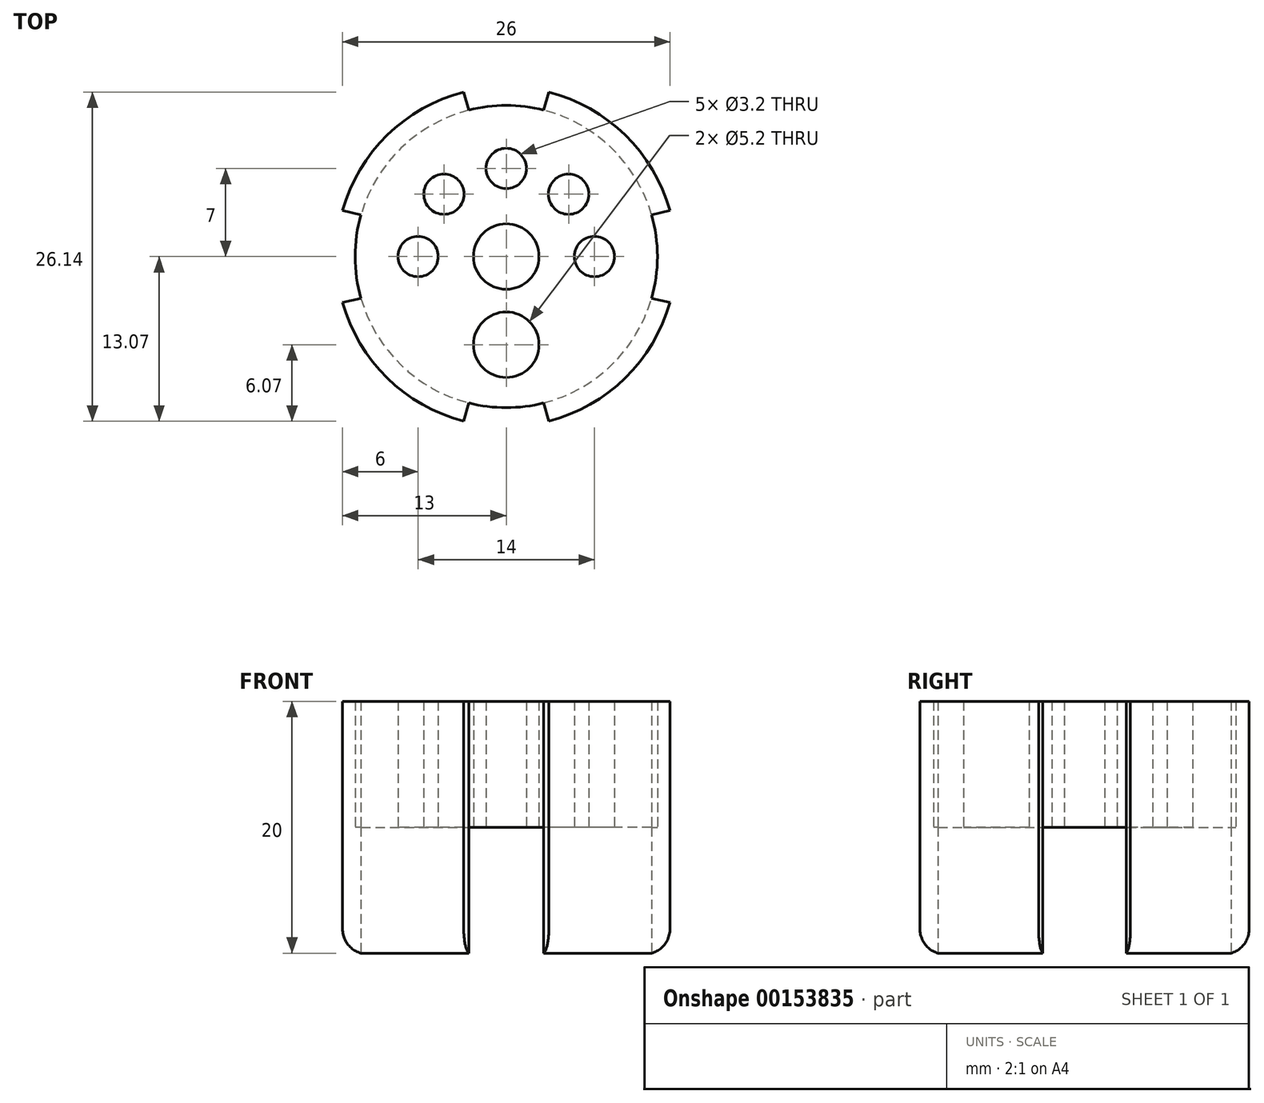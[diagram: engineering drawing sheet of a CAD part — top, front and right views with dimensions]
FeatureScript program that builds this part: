
annotation { "Feature Type Name" : "Feature", "Feature Type Description" : "" }
export const myFeature = defineFeature(function(context is Context, id is Id, definition is map)
    precondition{}
    {
        {
            var Q0;
            Q0=qCreatedBy(makeId("Top.planeOp"),FACE);
            var sketch = newSketch(context, id + "F0", { "sketchPlane" : qUnion([Q0])});
            skCircle(sketch, "E0", {"center": v(0, 0) * mm, "radius": 12 * mm});
            skCircle(sketch, "E1", {"center": v(0, 0) * mm, "radius": 10.25 * mm});
            skCircle(sketch, "E2", {"center": v(0, 0) * mm, "radius": 4.25 * mm});
            skCircle(sketch, "E3", {"center": v(0, 0) * mm, "radius": 2.6 * mm});
            skCircle(sketch, "E4", {"center": v(0, -7) * mm, "radius": 2.6 * mm});
            skCircle(sketch, "E5", {"center": v(0, 0) * mm, "radius": 7 * mm, "construction": true});
            skCircle(sketch, "E6", {"center": v(-7, 0) * mm, "radius": 1.6 * mm});
            skCircle(sketch, "E7", {"center": v(7, 0) * mm, "radius": 1.6 * mm});
            skCircle(sketch, "E8", {"center": v(0, 7) * mm, "radius": 1.6 * mm});
            skCircle(sketch, "E9", {"center": v(4.95, 4.95) * mm, "radius": 1.6 * mm});
            skCircle(sketch, "E10.MirrorC", {"center": v(-4.95, 4.95) * mm, "radius": 1.6 * mm});
            skCircle(sketch, "E11", {"center": v(0, 0) * mm, "radius": 13.5 * mm});
            skLineSegment(sketch, "E12", {"start": v(-3.38, 13.07) * mm, "end": v(-2.98, 11.62) * mm});
            skLineSegment(sketch, "E13", {"start": v(-13, 3.65) * mm, "end": v(-11.53, 3.32) * mm});
            skLineSegment(sketch, "E14.MirrorCS", {"start": v(3.38, 13.07) * mm, "end": v(2.98, 11.62) * mm});
            skLineSegment(sketch, "E15.MirrorCS", {"start": v(13, 3.65) * mm, "end": v(11.53, 3.32) * mm});
            skLineSegment(sketch, "E16.MirrorCS", {"start": v(-13, -3.65) * mm, "end": v(-11.53, -3.32) * mm});
            skLineSegment(sketch, "E17.MirrorCS", {"start": v(-3.38, -13.07) * mm, "end": v(-2.98, -11.62) * mm});
            skLineSegment(sketch, "E18.MirrorCS", {"start": v(3.38, -13.07) * mm, "end": v(2.98, -11.62) * mm});
            skLineSegment(sketch, "E19.MirrorCS", {"start": v(13, -3.65) * mm, "end": v(11.53, -3.32) * mm});
            skSolve(sketch);
        }
        {
            var Q0;
            Q0=makeQuery(id+"F0.imprint","IMPRINT",FACE,{"disambiguationData":[TD([[makeQuery(id+"F0.imprint","IMPRINT",EDGE,{"derivedFrom":sQuery(id+"F0.wireOp",EDGE,"E2")}),1.0]])]});
            extrude(context, id + "F1", {"entities" : qUnion([Q0]), "depth" : 10 * mm});
        }
        {
            var Q0;
            Q0=makeQuery(id+"F0.imprint","IMPRINT",FACE,{"disambiguationData":[TD([[makeQuery(id+"F0.imprint","IMPRINT",EDGE,{"derivedFrom":sQuery(id+"F0.wireOp",EDGE,"E1")}),1.0]])]});
            extrude(context, id + "F2", {"entities" : qUnion([Q0]), "operationType" : NewBodyOperationType.ADD, "depth" : 10 * mm});
        }
        {
            var Q0;
            Q0=makeQuery(id+"F0.imprint","IMPRINT",FACE,{"disambiguationData":[TD([[makeQuery(id+"F0.imprint","IMPRINT",EDGE,{"derivedFrom":sQuery(id+"F0.wireOp",EDGE,"E0")}),1.0]])]});
            extrude(context, id + "F3", {"entities" : qUnion([Q0]), "operationType" : NewBodyOperationType.ADD, "depth" : 10 * mm});
        }
        {
            var Q0;
            {var subQ0=sQuery(id+"F0.wireOp",EDGE,"E14.MirrorCS");Q0=makeQuery(id+"F0.imprint","IMPRINT",FACE,{"disambiguationData":[TD([[makeQuery(id+"F0.imprint","IMPRINT",EDGE,{"derivedFrom":subQ0}),1.0]])]});}
            var Q1;
            {var subQ0=sQuery(id+"F0.wireOp",EDGE,"E12");Q1=makeQuery(id+"F0.imprint","IMPRINT",FACE,{"disambiguationData":[TD([[makeQuery(id+"F0.imprint","IMPRINT",EDGE,{"derivedFrom":subQ0}),-1.0]])]});}
            var Q2;
            {var subQ0=sQuery(id+"F0.wireOp",EDGE,"E16.MirrorCS");Q2=makeQuery(id+"F0.imprint","IMPRINT",FACE,{"disambiguationData":[TD([[makeQuery(id+"F0.imprint","IMPRINT",EDGE,{"derivedFrom":subQ0}),-1.0]])]});}
            var Q3;
            {var subQ0=sQuery(id+"F0.wireOp",EDGE,"E18.MirrorCS");Q3=makeQuery(id+"F0.imprint","IMPRINT",FACE,{"disambiguationData":[TD([[makeQuery(id+"F0.imprint","IMPRINT",EDGE,{"derivedFrom":subQ0}),-1.0]])]});}
            extrude(context, id + "F4", {"entities" : qUnion([Q0, Q1, Q2, Q3]), "operationType" : NewBodyOperationType.ADD, "endBound" : BoundingType.SYMMETRIC, "depth" : 20 * mm});
        }
        {
            var Q0;
            {var subQ0=sQuery(id+"F0.wireOp",EDGE,"E11");Q0=makeQuery(id+"F4.opExtrude","CAP_EDGE",EDGE,{"disambiguationData":[OSD([subQ0]),TDD([makeQuery(id+"F0.imprint","IMPRINT",EDGE,{"disambiguationData":[TD([[makeQuery(id+"F0.imprint","INTERSECT",VERTEX,{"derivedFrom":[subQ0,sQuery(id+"F0.wireOp",EDGE,"E14.MirrorCS")]}),1.0]])],"derivedFrom":subQ0})])],"isStart":true});}
            var Q1;
            {var subQ0=sQuery(id+"F0.wireOp",EDGE,"E11");Q1=makeQuery(id+"F4.opExtrude","CAP_EDGE",EDGE,{"disambiguationData":[OSD([subQ0]),TDD([makeQuery(id+"F0.imprint","IMPRINT",EDGE,{"disambiguationData":[TD([[makeQuery(id+"F0.imprint","INTERSECT",VERTEX,{"derivedFrom":[subQ0,sQuery(id+"F0.wireOp",EDGE,"E12")]}),-1.0]])],"derivedFrom":subQ0})])],"isStart":true});}
            var Q2;
            {var subQ0=sQuery(id+"F0.wireOp",EDGE,"E11");Q2=makeQuery(id+"F4.opExtrude","CAP_EDGE",EDGE,{"disambiguationData":[OSD([subQ0]),TDD([makeQuery(id+"F0.imprint","IMPRINT",EDGE,{"disambiguationData":[TD([[makeQuery(id+"F0.imprint","INTERSECT",VERTEX,{"derivedFrom":[subQ0,sQuery(id+"F0.wireOp",EDGE,"E16.MirrorCS")]}),-1.0]])],"derivedFrom":subQ0})])],"isStart":true});}
            var Q3;
            {var subQ0=sQuery(id+"F0.wireOp",EDGE,"E11");Q3=makeQuery(id+"F4.opExtrude","CAP_EDGE",EDGE,{"disambiguationData":[OSD([subQ0]),TDD([makeQuery(id+"F0.imprint","IMPRINT",EDGE,{"disambiguationData":[TD([[makeQuery(id+"F0.imprint","INTERSECT",VERTEX,{"derivedFrom":[subQ0,sQuery(id+"F0.wireOp",EDGE,"E18.MirrorCS")]}),-1.0]])],"derivedFrom":subQ0})])],"isStart":true});}
            fillet(context, id + "F5", {"entities" : qUnion([Q0, Q1, Q2, Q3]), "radius" : 2 * mm, "tangentPropagation" : true, "allowEdgeOverflow" : false});
        }
    });
